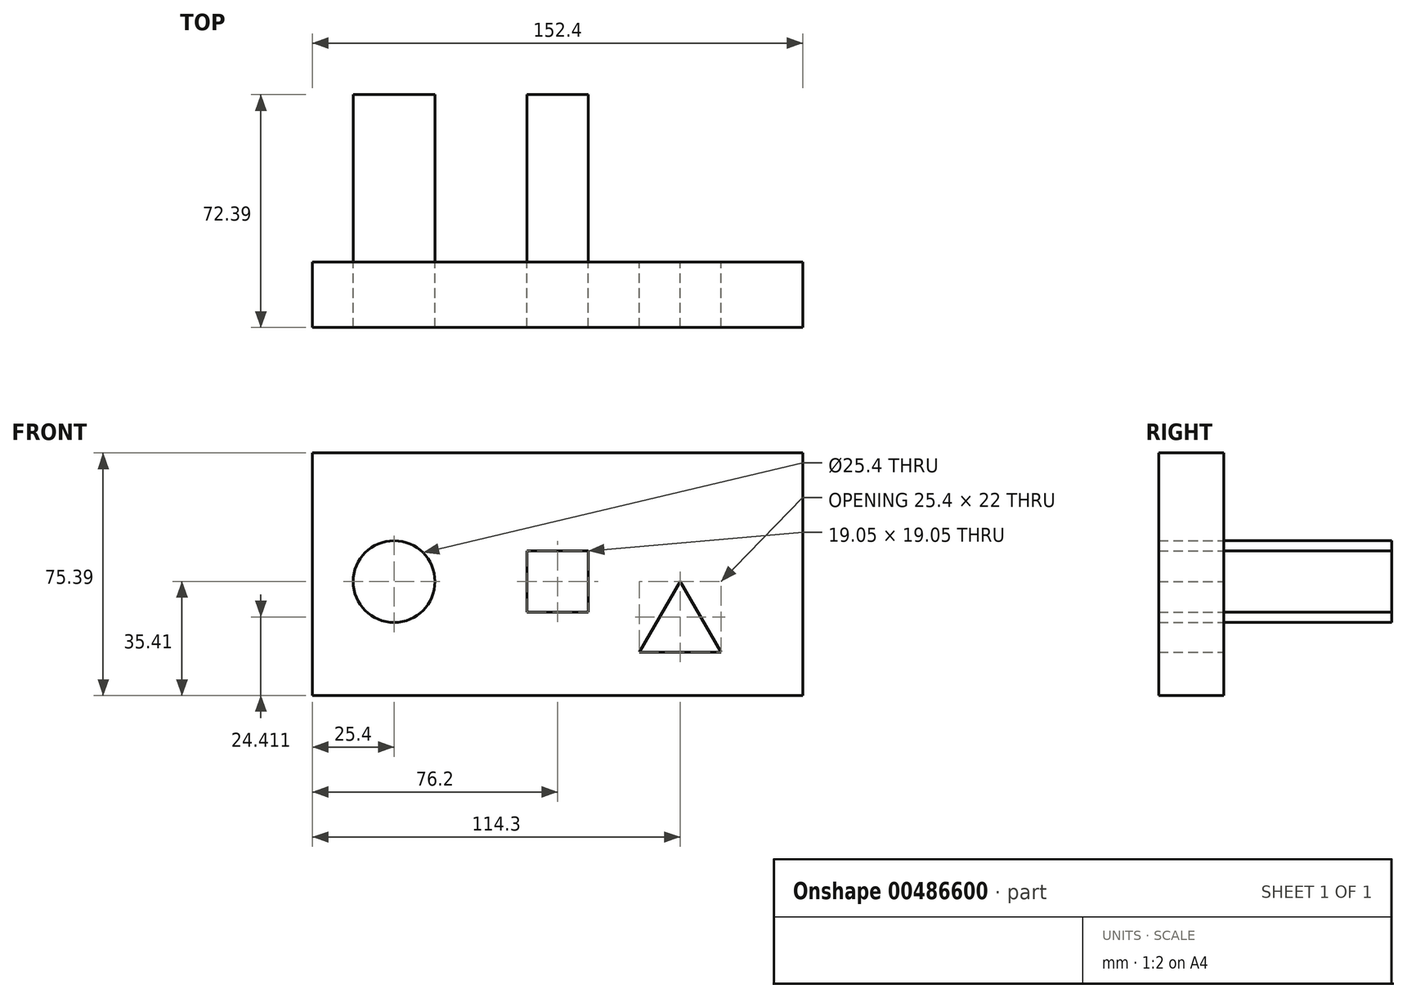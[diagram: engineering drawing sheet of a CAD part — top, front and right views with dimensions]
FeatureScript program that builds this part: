
annotation { "Feature Type Name" : "Feature", "Feature Type Description" : "" }
export const myFeature = defineFeature(function(context is Context, id is Id, definition is map)
    precondition{}
    {
        {
            var Q0;
            Q0=qCreatedBy(makeId("Front.planeOp"),FACE);
            var sketch = newSketch(context, id + "F0", { "sketchPlane" : qUnion([Q0])});
            skLineSegment(sketch, "E0", {"start": v(0, 0) * mm, "end": v(6.35, 0) * mm});
            skLineSegment(sketch, "E1", {"start": v(6.35, 0) * mm, "end": v(-6.35, -22) * mm});
            skLineSegment(sketch, "E2", {"start": v(-6.35, -22) * mm, "end": v(19.05, -22) * mm});
            skLineSegment(sketch, "E3", {"start": v(19.05, -22) * mm, "end": v(6.35, 0) * mm});
            skLineSegment(sketch, "E4", {"start": v(0, 0) * mm, "end": v(-31.75, 0) * mm});
            skLineSegment(sketch, "E5.bottom", {"start": v(-41.27, 9.52) * mm, "end": v(-22.22, 9.52) * mm});
            skLineSegment(sketch, "E5.top", {"start": v(-41.28, -9.53) * mm, "end": v(-22.22, -9.53) * mm});
            skLineSegment(sketch, "E5.left", {"start": v(-41.28, 9.52) * mm, "end": v(-41.28, -9.53) * mm});
            skLineSegment(sketch, "E5.right", {"start": v(-22.22, 9.52) * mm, "end": v(-22.23, -9.53) * mm});
            skPoint(sketch, "E5.middle", {"position": v(-31.75, 0) * mm});
            skLineSegment(sketch, "E6", {"start": v(-31.75, 0) * mm, "end": v(-82.55, 0) * mm});
            skPoint(sketch, "E6.endSnap0", {"position": v(-41.28, 0) * mm});
            skCircle(sketch, "E7", {"center": v(-82.55, 0) * mm, "radius": 12.7 * mm});
            skLineSegment(sketch, "E8", {"start": v(0, -35.41) * mm, "end": v(44.45, -35.41) * mm});
            skLineSegment(sketch, "E9.bottom", {"start": v(44.45, -35.41) * mm, "end": v(-107.95, -35.41) * mm});
            skLineSegment(sketch, "E9.top", {"start": v(44.45, 39.98) * mm, "end": v(-107.95, 39.98) * mm});
            skLineSegment(sketch, "E9.left", {"start": v(44.45, -35.41) * mm, "end": v(44.45, 39.98) * mm});
            skLineSegment(sketch, "E9.right", {"start": v(-107.95, -35.41) * mm, "end": v(-107.95, 39.98) * mm});
            skSolve(sketch);
        }
        {
            var Q0;
            Q0=makeQuery(id+"F0.imprint","IMPRINT",FACE,{"disambiguationData":[TD([[makeQuery(id+"F0.imprint","IMPRINT",EDGE,{"derivedFrom":sQuery(id+"F0.wireOp",EDGE,"E7")}),1.0]])]});
            var Q1;
            {var subQ1=sQuery(id+"F0.wireOp",EDGE,"E5.bottom");Q1=makeQuery(id+"F0.imprint","IMPRINT",FACE,{"disambiguationData":[TD([[makeQuery(id+"F0.imprint","IMPRINT",EDGE,{"derivedFrom":subQ1}),-1.0]])]});}
            var Q2;
            {var subQ1=sQuery(id+"F0.wireOp",EDGE,"E5.top");Q2=makeQuery(id+"F0.imprint","IMPRINT",FACE,{"disambiguationData":[TD([[makeQuery(id+"F0.imprint","IMPRINT",EDGE,{"derivedFrom":subQ1}),1.0]])]});}
            extrude(context, id + "F1", {"entities" : qUnion([Q0, Q1, Q2]), "oppositeDirection" : true, "depth" : 52.07 * mm});
        }
        {
            var Q0;
            Q0 = qSketchRegion(id + "F0", true);
            extrude(context, id + "F2", {"entities" : qUnion([Q0]), "depth" : 20.32 * mm});
        }
    });
